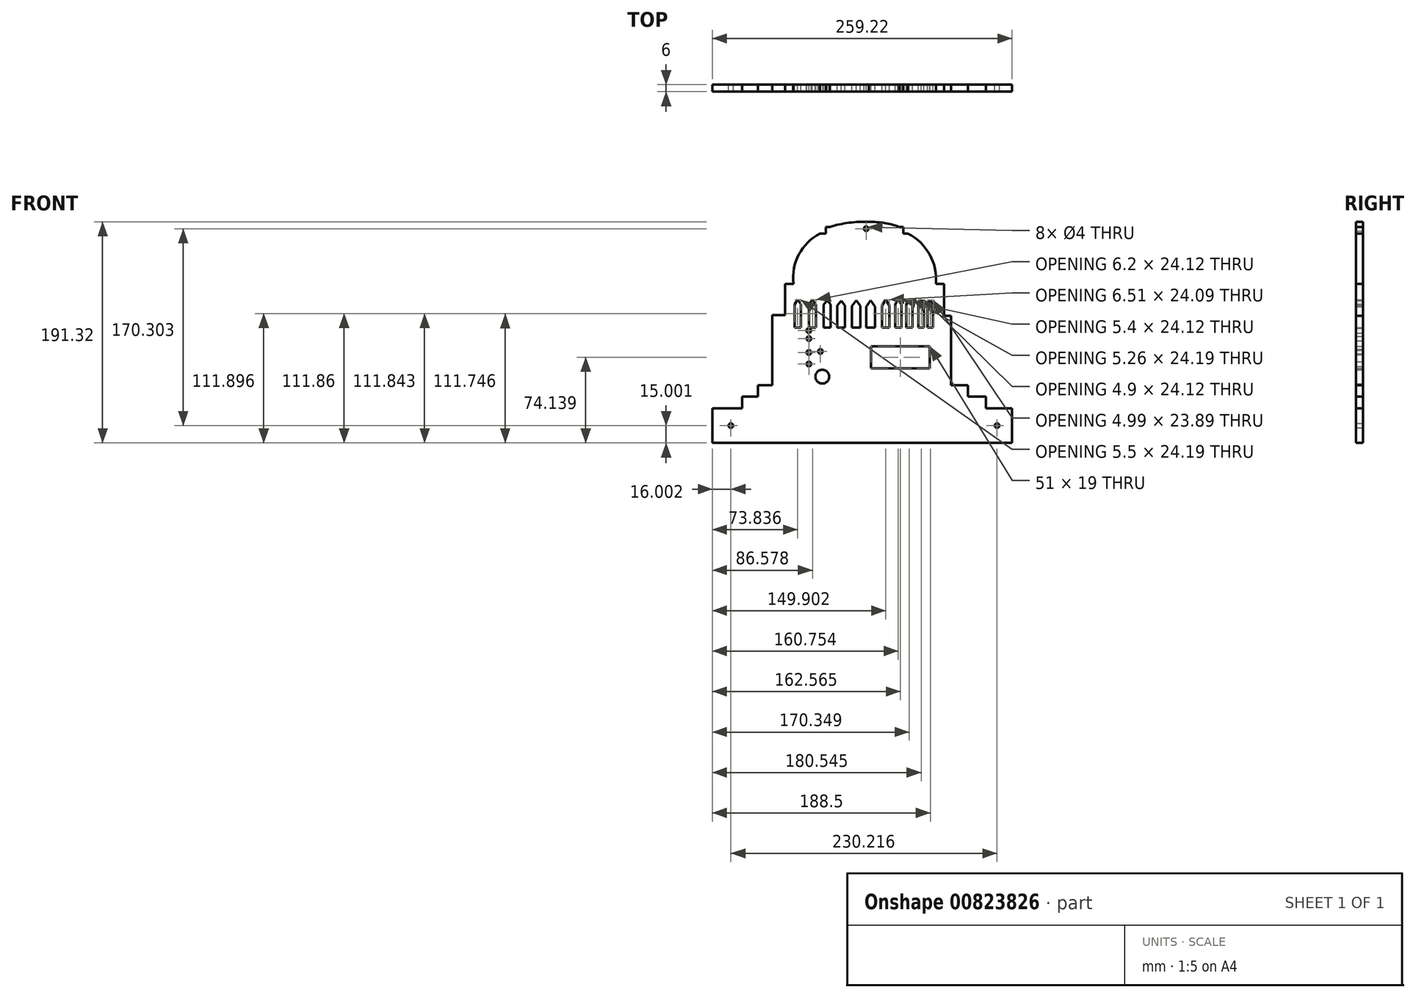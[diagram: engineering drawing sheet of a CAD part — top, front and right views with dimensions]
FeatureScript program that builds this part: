
annotation { "Feature Type Name" : "Feature", "Feature Type Description" : "" }
export const myFeature = defineFeature(function(context is Context, id is Id, definition is map)
    precondition{}
    {
        {
            var Q0;
            Q0=qCreatedBy(makeId("Front.planeOp"),FACE);
            var sketch = newSketch(context, id + "F0", { "sketchPlane" : qUnion([Q0])});
            skLineSegment(sketch, "E0.bottom", {"start": v(0, 0) * mm, "end": v(300, 0) * mm, "construction": true});
            skLineSegment(sketch, "E0.top", {"start": v(0, -200) * mm, "end": v(300, -200) * mm, "construction": true});
            skLineSegment(sketch, "E0.left", {"start": v(0, 0) * mm, "end": v(0, -200) * mm, "construction": true});
            skLineSegment(sketch, "E0.right", {"start": v(300, 0) * mm, "end": v(300, -200) * mm, "construction": true});
            skLineSegment(sketch, "E1.bottom", {"start": v(26.58, -161.25) * mm, "end": v(285.8, -161.25) * mm});
            skLineSegment(sketch, "E1.top", {"start": v(26.58, -191.25) * mm, "end": v(285.8, -191.25) * mm});
            skLineSegment(sketch, "E1.left", {"start": v(26.58, -161.25) * mm, "end": v(26.58, -191.25) * mm});
            skLineSegment(sketch, "E1.right", {"start": v(285.8, -161.25) * mm, "end": v(285.8, -191.25) * mm});
            skLineSegment(sketch, "E2", {"start": v(52.47, -161.25) * mm, "end": v(52.47, -151.05) * mm});
            skLineSegment(sketch, "E3", {"start": v(52.47, -151.05) * mm, "end": v(263.24, -151.05) * mm});
            skLineSegment(sketch, "E4", {"start": v(263.24, -151.05) * mm, "end": v(263.24, -161.25) * mm});
            skLineSegment(sketch, "E5", {"start": v(66.05, -151.05) * mm, "end": v(66.05, -141.45) * mm});
            skLineSegment(sketch, "E6", {"start": v(66.05, -141.45) * mm, "end": v(247.49, -141.45) * mm});
            skLineSegment(sketch, "E7", {"start": v(247.49, -141.45) * mm, "end": v(247.49, -151.05) * mm});
            skLineSegment(sketch, "E8", {"start": v(233, -141.45) * mm, "end": v(233, -81.45) * mm});
            skLineSegment(sketch, "E9", {"start": v(78.36, -141.45) * mm, "end": v(78.36, -80.77) * mm});
            skLineSegment(sketch, "E10", {"start": v(233, -81.45) * mm, "end": v(227, -81.45) * mm});
            skLineSegment(sketch, "E11", {"start": v(227, -81.45) * mm, "end": v(227, -53.72) * mm});
            skLineSegment(sketch, "E12", {"start": v(89.6, -80.77) * mm, "end": v(89.6, -53.62) * mm});
            skLineSegment(sketch, "E13", {"start": v(89.6, -53.62) * mm, "end": v(96.73, -53.62) * mm});
            skLineSegment(sketch, "E14", {"start": v(97.67, -91.45) * mm, "end": v(221.46, -91.45) * mm});
            skLineSegment(sketch, "E15", {"start": v(106.84, -91.45) * mm, "end": v(106.84, -91.45) * mm});
            skLineSegment(sketch, "E16", {"start": v(110.06, -91.45) * mm, "end": v(110.06, -71.59) * mm});
            skLineSegment(sketch, "E17", {"start": v(116.26, -71.59) * mm, "end": v(116.26, -91.45) * mm});
            skLineSegment(sketch, "E18", {"start": v(122.72, -91.45) * mm, "end": v(122.72, -71.56) * mm});
            skLineSegment(sketch, "E19", {"start": v(122.72, -71.56) * mm, "end": v(126.06, -68.06) * mm});
            skLineSegment(sketch, "E20", {"start": v(126.06, -68.06) * mm, "end": v(128.81, -71.56) * mm});
            skLineSegment(sketch, "E21", {"start": v(128.81, -71.56) * mm, "end": v(128.81, -91.45) * mm});
            skLineSegment(sketch, "E22", {"start": v(134.7, -91.45) * mm, "end": v(134.7, -72.43) * mm});
            skLineSegment(sketch, "E23", {"start": v(134.7, -72.43) * mm, "end": v(138.06, -68.22) * mm});
            skLineSegment(sketch, "E24", {"start": v(138.06, -68.22) * mm, "end": v(141.38, -72.43) * mm});
            skLineSegment(sketch, "E25", {"start": v(141.38, -72.43) * mm, "end": v(141.38, -91.45) * mm});
            skLineSegment(sketch, "E26", {"start": v(147.32, -91.45) * mm, "end": v(147.32, -72.64) * mm});
            skLineSegment(sketch, "E27", {"start": v(147.32, -72.64) * mm, "end": v(151.1, -67.91) * mm});
            skLineSegment(sketch, "E28", {"start": v(151.1, -67.91) * mm, "end": v(154.6, -72.64) * mm});
            skLineSegment(sketch, "E29", {"start": v(154.6, -72.64) * mm, "end": v(154.6, -91.45) * mm});
            skPoint(sketch, "E30", {"position": v(151.1, -63.83) * mm});
            skLineSegment(sketch, "E31", {"start": v(159.6, -91.45) * mm, "end": v(159.6, -73.28) * mm});
            skLineSegment(sketch, "E32", {"start": v(159.6, -73.28) * mm, "end": v(163.57, -68.1) * mm});
            skLineSegment(sketch, "E33", {"start": v(163.57, -68.1) * mm, "end": v(167.2, -73.28) * mm});
            skLineSegment(sketch, "E34", {"start": v(167.2, -73.28) * mm, "end": v(167.2, -91.45) * mm});
            skLineSegment(sketch, "E35", {"start": v(173.23, -91.45) * mm, "end": v(173.23, -72.41) * mm});
            skLineSegment(sketch, "E36", {"start": v(173.23, -72.41) * mm, "end": v(176.39, -67.36) * mm});
            skLineSegment(sketch, "E37", {"start": v(176.39, -67.36) * mm, "end": v(179.74, -72.41) * mm});
            skLineSegment(sketch, "E38", {"start": v(179.74, -72.41) * mm, "end": v(179.74, -91.45) * mm});
            skPoint(sketch, "E39.start.orphan", {"position": v(198.04, -6.46) * mm});
            skLineSegment(sketch, "E40", {"start": v(163.65, -107.61) * mm, "end": v(214.65, -107.61) * mm});
            skLineSegment(sketch, "E41", {"start": v(163.65, -107.61) * mm, "end": v(163.65, -126.61) * mm});
            skLineSegment(sketch, "E42", {"start": v(163.65, -126.61) * mm, "end": v(214.65, -126.61) * mm});
            skLineSegment(sketch, "E43", {"start": v(214.65, -107.61) * mm, "end": v(214.65, -126.61) * mm});
            skLineSegment(sketch, "E44", {"start": v(227, -53.72) * mm, "end": v(198.04, -53.97) * mm});
            skLineSegment(sketch, "E45", {"start": v(110.06, -71.59) * mm, "end": v(112.95, -67.33) * mm});
            skLineSegment(sketch, "E46", {"start": v(116.26, -71.59) * mm, "end": v(112.95, -67.33) * mm});
            skLineSegment(sketch, "E47", {"start": v(184.64, -91.45) * mm, "end": v(184.64, -71.59) * mm});
            skLineSegment(sketch, "E48", {"start": v(184.64, -71.59) * mm, "end": v(186.98, -67.33) * mm});
            skLineSegment(sketch, "E49", {"start": v(186.98, -67.33) * mm, "end": v(190.03, -71.59) * mm});
            skLineSegment(sketch, "E50", {"start": v(190.03, -71.59) * mm, "end": v(190.03, -91.45) * mm});
            skLineSegment(sketch, "E51", {"start": v(204.67, -91.45) * mm, "end": v(204.67, -71.59) * mm});
            skLineSegment(sketch, "E52", {"start": v(204.67, -71.59) * mm, "end": v(207.25, -67.33) * mm});
            skLineSegment(sketch, "E53", {"start": v(207.25, -67.33) * mm, "end": v(209.58, -71.59) * mm});
            skLineSegment(sketch, "E54", {"start": v(209.58, -71.59) * mm, "end": v(209.58, -91.45) * mm});
            skLineSegment(sketch, "E55", {"start": v(194.3, -91.45) * mm, "end": v(194.3, -71.59) * mm});
            skLineSegment(sketch, "E56", {"start": v(199.56, -71.59) * mm, "end": v(199.56, -91.45) * mm});
            skLineSegment(sketch, "E57", {"start": v(96.73, -53.62) * mm, "end": v(198.04, -53.97) * mm});
            skCircle(sketch, "E58", {"center": v(121.65, -133.9) * mm, "radius": 6 * mm});
            skLineSegment(sketch, "E59", {"start": v(194.3, -71.59) * mm, "end": v(196.84, -67.26) * mm});
            skLineSegment(sketch, "E60", {"start": v(196.84, -67.26) * mm, "end": v(199.56, -71.59) * mm});
            skLineSegment(sketch, "E61", {"start": v(212.59, -91.45) * mm, "end": v(212.59, -71.51) * mm});
            skLineSegment(sketch, "E62", {"start": v(212.59, -71.51) * mm, "end": v(214.83, -67.56) * mm});
            skLineSegment(sketch, "E63", {"start": v(214.83, -67.56) * mm, "end": v(217.57, -71.28) * mm});
            skLineSegment(sketch, "E64", {"start": v(217.57, -71.28) * mm, "end": v(217.57, -91.45) * mm});
            skLineSegment(sketch, "E65", {"start": v(221.46, -91.45) * mm, "end": v(227, -81.45) * mm});
            skArc(sketch, "E66", {"start": v(219.92, -53.78) * mm, "mid": v(214.48, -28.24) * mm, "end": v(195.62, -10.18) * mm});
            skArc(sketch, "E67", {"start": v(119.7, -10.18) * mm, "mid": v(101.37, -28.28) * mm, "end": v(96.73, -53.62) * mm});
            skLineSegment(sketch, "E68", {"start": v(78.36, -80.77) * mm, "end": v(89.6, -80.77) * mm});
            skLineSegment(sketch, "E69", {"start": v(89.6, -80.77) * mm, "end": v(97.67, -91.45) * mm});
            skPoint(sketch, "E70.orphan", {"position": v(89.6, -91.45) * mm});
            skLineSegment(sketch, "E71", {"start": v(97.67, -91.45) * mm, "end": v(97.67, -71.49) * mm});
            skLineSegment(sketch, "E72", {"start": v(97.67, -71.49) * mm, "end": v(100.13, -67.26) * mm});
            skLineSegment(sketch, "E73", {"start": v(100.13, -67.26) * mm, "end": v(103.17, -71.28) * mm});
            skLineSegment(sketch, "E74", {"start": v(103.17, -71.28) * mm, "end": v(103.17, -91.45) * mm});
            skLineSegment(sketch, "E75", {"start": v(119.7, -10.18) * mm, "end": v(124.78, -10.18) * mm});
            skLineSegment(sketch, "E76", {"start": v(124.78, -10.18) * mm, "end": v(124.78, -4.34) * mm});
            skLineSegment(sketch, "E77", {"start": v(191.7, -4.34) * mm, "end": v(191.7, -10.18) * mm});
            skArc(sketch, "E78", {"start": v(161.99, 0) * mm, "mid": v(144.87, -0.79) * mm, "end": v(128.1, -4.34) * mm});
            skArc(sketch, "E79", {"start": v(188.15, -4.34) * mm, "mid": v(175.26, -1) * mm, "end": v(161.99, 0) * mm});
            skLineSegment(sketch, "E80.trimOffspring", {"start": v(191.7, -10.18) * mm, "end": v(195.62, -10.18) * mm});
            skLineSegment(sketch, "E81", {"start": v(124.78, -4.34) * mm, "end": v(128.1, -4.34) * mm});
            skLineSegment(sketch, "E82", {"start": v(191.7, -4.34) * mm, "end": v(188.15, -4.34) * mm});
            skCircle(sketch, "E83", {"center": v(110.06, -123.02) * mm, "radius": 2 * mm});
            skCircle(sketch, "E84", {"center": v(110.06, -113.02) * mm, "radius": 2 * mm});
            skCircle(sketch, "E85", {"center": v(110.06, -101.02) * mm, "radius": 2 * mm});
            skCircle(sketch, "E86", {"center": v(109.93, -94.1) * mm, "radius": 2 * mm});
            skCircle(sketch, "E87", {"center": v(120.02, -112.12) * mm, "radius": 2 * mm});
            skCircle(sketch, "E88", {"center": v(42.58, -176.25) * mm, "radius": 2 * mm});
            skCircle(sketch, "E89", {"center": v(272.8, -176.25) * mm, "radius": 2 * mm});
            skCircle(sketch, "E90", {"center": v(159.58, -5.95) * mm, "radius": 2 * mm});
            skSolve(sketch);
        }
        {
            var Q0;
            Q0 = qSketchRegion(id + "F0", true);
            extrude(context, id + "F1", {"entities" : qUnion([Q0]), "depth" : 3 * mm, "offsetDistance" : 25 * mm, "hasSecondDirection" : true, "secondDirectionOppositeDirection" : true, "secondDirectionDepth" : 3 * mm});
        }
        {
            var Q0;
            Q0 = qSketchRegion(id + "F0", true);
            extrude(context, id + "F2", {"entities" : qUnion([Q0]), "operationType" : NewBodyOperationType.ADD, "depth" : 3 * mm, "offsetDistance" : 25 * mm});
        }
    });
